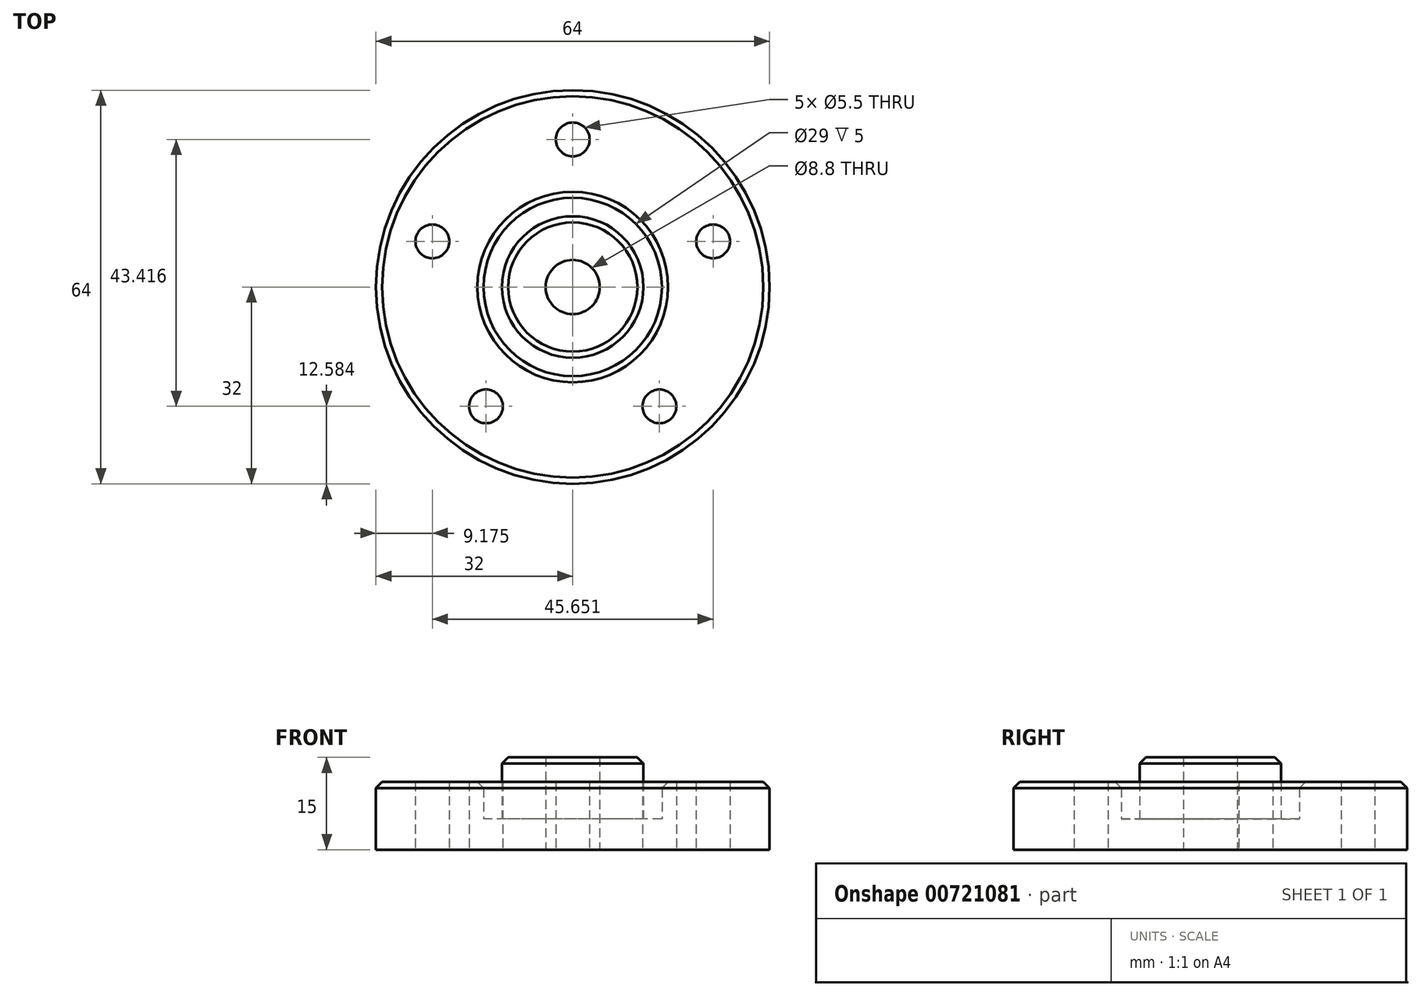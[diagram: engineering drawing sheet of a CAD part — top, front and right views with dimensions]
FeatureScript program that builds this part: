
annotation { "Feature Type Name" : "Feature", "Feature Type Description" : "" }
export const myFeature = defineFeature(function(context is Context, id is Id, definition is map)
    precondition{}
    {
        {
            var Q0;
            Q0=qCreatedBy(makeId("Top.planeOp"),FACE);
            var sketch = newSketch(context, id + "F0", { "sketchPlane" : qUnion([Q0])});
            skCircle(sketch, "E0", {"center": v(0, 0) * mm, "radius": 11.5 * mm});
            skCircle(sketch, "E1", {"center": v(0, 0) * mm, "radius": 14.5 * mm});
            skCircle(sketch, "E2", {"center": v(0, 0) * mm, "radius": 32 * mm});
            skPoint(sketch, "E3", {"position": v(0, 24) * mm});
            skPoint(sketch, "E4.1.0", {"position": v(-22.83, 7.42) * mm});
            skPoint(sketch, "E4.2.0", {"position": v(-14.1, -19.42) * mm});
            skPoint(sketch, "E4.3.0", {"position": v(14.1, -19.42) * mm});
            skPoint(sketch, "E4.4.0", {"position": v(22.83, 7.42) * mm});
            skSolve(sketch);
        }
        {
            var Q0;
            Q0=makeQuery(id+"F0.imprint","IMPRINT",FACE,{"disambiguationData":[TD([[makeQuery(id+"F0.imprint","IMPRINT",EDGE,{"derivedFrom":sQuery(id+"F0.wireOp",EDGE,"E0")}),1.0]])]});
            extrude(context, id + "F1", {"entities" : qUnion([Q0]), "depth" : 15 * mm, "offsetDistance" : 25 * mm});
        }
        {
            var Q0;
            Q0=makeQuery(id+"F0.imprint","IMPRINT",FACE,{"disambiguationData":[TD([[makeQuery(id+"F0.imprint","IMPRINT",EDGE,{"derivedFrom":sQuery(id+"F0.wireOp",EDGE,"E0")}),-1.0]])]});
            extrude(context, id + "F2", {"entities" : qUnion([Q0]), "operationType" : NewBodyOperationType.ADD, "depth" : 5 * mm, "offsetDistance" : 25 * mm});
        }
        {
            var Q0;
            Q0=makeQuery(id+"F0.imprint","IMPRINT",FACE,{"disambiguationData":[TD([[makeQuery(id+"F0.imprint","IMPRINT",EDGE,{"derivedFrom":sQuery(id+"F0.wireOp",EDGE,"E1")}),-1.0]])]});
            extrude(context, id + "F3", {"entities" : qUnion([Q0]), "operationType" : NewBodyOperationType.ADD, "depth" : 11 * mm, "offsetDistance" : 25 * mm});
        }
        {
            var Q0;
            Q0=sQuery(id+"F0.wireOp",VERTEX,"E4.1.0");
            var Q1;
            Q1=sQuery(id+"F0.wireOp",VERTEX,"E3");
            var Q2;
            Q2=sQuery(id+"F0.wireOp",VERTEX,"E4.4.0");
            var Q3;
            Q3=sQuery(id+"F0.wireOp",VERTEX,"E4.3.0");
            var Q4;
            Q4=sQuery(id+"F0.wireOp",VERTEX,"E4.2.0");
            var Q5;
            Q5=makeQuery(id+"F1.opExtrude","SWEPT_BODY",BODY,{"disambiguationData":[OSD([sQuery(id+"F0.wireOp",EDGE,"E0")])]});
            hole(context, id + "F4", {"style" : HoleStyle.SIMPLE, "endStyle" : HoleEndStyle.THROUGH, "oppositeDirection" : true, "standardTappedOrClearance" : lookupTablePath({ "standard" : "ISO", "fit" : "Normal", "size" : "M5", "type" : "Clearance" }), "standardBlindInLast" : lookupTablePath({ "fit" : "Standard", "standard" : "ISO", "size" : "M5", "type" : "Clearance" }), "holeDiameter" : 5.5 * mm, "majorDiameter" : 5 * mm, "isTappedThrough" : true, "tappedDepth" : 12 * mm, "tapClearance" : 3, "locations" : qUnion([Q0, Q1, Q2, Q3, Q4]), "scope" : qUnion([Q5])});
        }
        {
            var Q0;
            Q0=sQuery(id+"F0.wireOp",VERTEX,"E0.center");
            var Q1;
            Q1=makeQuery(id+"F1.opExtrude","SWEPT_BODY",BODY,{"disambiguationData":[OSD([sQuery(id+"F0.wireOp",EDGE,"E0")])]});
            hole(context, id + "F5", {"style" : HoleStyle.SIMPLE, "endStyle" : HoleEndStyle.THROUGH, "oppositeDirection" : true, "standardTappedOrClearance" : lookupTablePath({ "standard" : "ISO", "fit" : "Normal", "size" : "M8", "type" : "Clearance" }), "standardBlindInLast" : lookupTablePath({ "fit" : "Standard", "standard" : "ISO", "size" : "M8", "type" : "Clearance" }), "holeDiameter" : 8.8 * mm, "majorDiameter" : 5 * mm, "isTappedThrough" : true, "tappedDepth" : 12 * mm, "tapClearance" : 3, "locations" : qUnion([Q0]), "scope" : qUnion([Q1])});
        }
        {
            var Q0;
            Q0=makeQuery(id+"F1.opExtrude","CAP_EDGE",EDGE,{"disambiguationData":[OSD([sQuery(id+"F0.wireOp",EDGE,"E0")])],"isStart":false});
            chamfer(context, id + "F6", {"entities" : qUnion([Q0]), "width" : 1 * mm, "tangentPropagation" : true});
        }
        {
            var Q0;
            Q0=makeQuery(id+"F3.opExtrude","CAP_EDGE",EDGE,{"disambiguationData":[OSD([sQuery(id+"F0.wireOp",EDGE,"E1")])],"isStart":false});
            chamfer(context, id + "F7", {"entities" : qUnion([Q0]), "width" : 1 * mm, "tangentPropagation" : true});
        }
        {
            var Q0;
            Q0=makeQuery(id+"F3.opExtrude","CAP_EDGE",EDGE,{"disambiguationData":[OSD([sQuery(id+"F0.wireOp",EDGE,"E2")])],"isStart":false});
            chamfer(context, id + "F8", {"entities" : qUnion([Q0]), "width" : 1 * mm, "tangentPropagation" : true});
        }
    });
